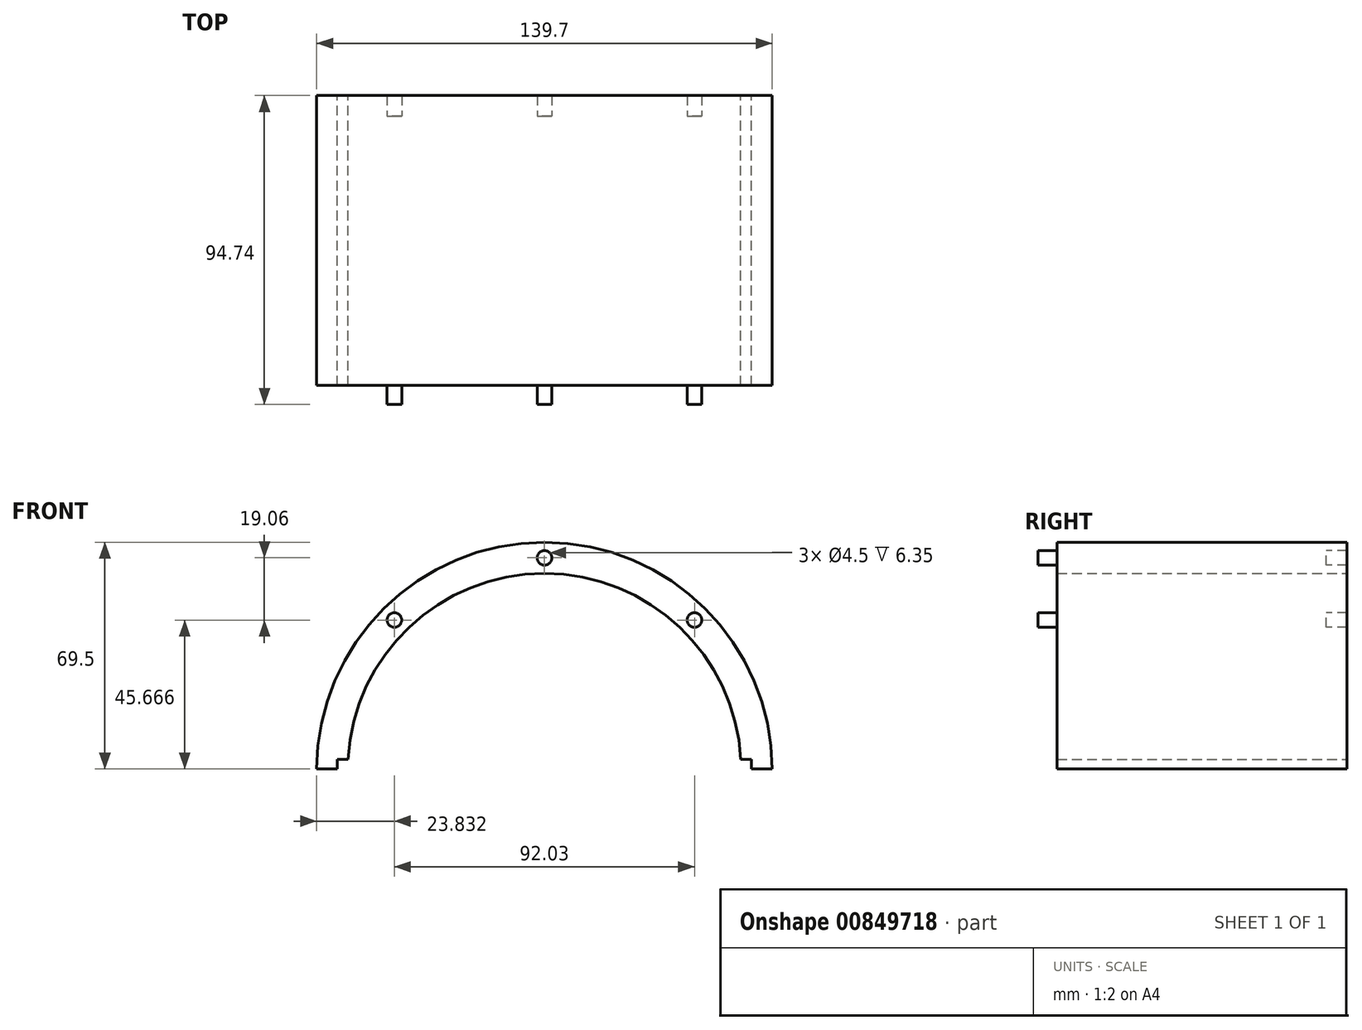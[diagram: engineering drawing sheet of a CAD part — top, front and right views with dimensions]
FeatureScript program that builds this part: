
annotation { "Feature Type Name" : "Feature", "Feature Type Description" : "" }
export const myFeature = defineFeature(function(context is Context, id is Id, definition is map)
    precondition{}
    {
        {
            var Q0;
            Q0=qCreatedBy(makeId("Front.planeOp"),FACE);
            var sketch = newSketch(context, id + "F0", { "sketchPlane" : qUnion([Q0])});
            skArc(sketch, "E0", {"start": v(33.34, 8.81) * mm, "mid": v(-36.51, 78.31) * mm, "end": v(-106.36, 8.81) * mm});
            skArc(sketch, "E1", {"start": v(23.72, 11.78) * mm, "mid": v(-36.51, 68.79) * mm, "end": v(-96.75, 11.78) * mm});
            skLineSegment(sketch, "E2.trimOffspring", {"start": v(26.98, 8.81) * mm, "end": v(33.34, 8.81) * mm});
            skLineSegment(sketch, "E3.left", {"start": v(-100, 11.78) * mm, "end": v(-100, 8.81) * mm});
            skLineSegment(sketch, "E4", {"start": v(-100, 11.78) * mm, "end": v(-96.75, 11.78) * mm});
            skLineSegment(sketch, "E5.right", {"start": v(26.98, 8.81) * mm, "end": v(26.98, 11.78) * mm});
            skLineSegment(sketch, "E6", {"start": v(-106.36, 8.81) * mm, "end": v(-100, 8.81) * mm});
            skPoint(sketch, "E7.orphan", {"position": v(27.73, 11.78) * mm});
            skLineSegment(sketch, "E8", {"start": v(26.98, 11.78) * mm, "end": v(23.72, 11.78) * mm});
            skLineSegment(sketch, "E9", {"start": v(26.98, 11.78) * mm, "end": v(33.26, 11.78) * mm});
            skLineSegment(sketch, "E10", {"start": v(-100, 11.78) * mm, "end": v(-106.28, 11.78) * mm});
            skLineSegment(sketch, "E11", {"start": v(26.98, 8.81) * mm, "end": v(-100, 8.81) * mm});
            skArc(sketch, "E12", {"start": v(30.16, 8.81) * mm, "mid": v(-36.51, 75.14) * mm, "end": v(-103.19, 8.81) * mm});
            skSolve(sketch);
        }
        {
            var Q0;
            Q0=makeQuery(id+"F0.imprint","IMPRINT",FACE,{"disambiguationData":[TD([[makeQuery(id+"F0.imprint","IMPRINT",EDGE,{"derivedFrom":sQuery(id+"F0.wireOp",EDGE,"E1")}),-1.0]])]});
            var Q1;
            Q1=makeQuery(id+"F0.imprint","IMPRINT",FACE,{"disambiguationData":[TD([[makeQuery(id+"F0.imprint","IMPRINT",EDGE,{"derivedFrom":sQuery(id+"F0.wireOp",EDGE,"E3.left")}),-1.0]])]});
            var Q2;
            {var subQ0=sQuery(id+"F0.wireOp",EDGE,"E2.trimOffspring");Q2=makeQuery(id+"F0.imprint","IMPRINT",FACE,{"disambiguationData":[TD([[makeQuery(id+"F0.imprint","IMPRINT",EDGE,{"derivedFrom":subQ0}),1.0]])]});}
            var Q3;
            {var subQ0=sQuery(id+"F0.wireOp",EDGE,"E9");var subQ1=sQuery(id+"F0.wireOp",EDGE,"E0");var subQ2=makeQuery(id+"F0.imprint","INTERSECT",VERTEX,{"derivedFrom":[subQ1,subQ0]});Q3=makeQuery(id+"F0.imprint","IMPRINT",FACE,{"disambiguationData":[TD([[makeQuery(id+"F0.imprint","IMPRINT",EDGE,{"disambiguationData":[TD([[subQ2,-1.0]])],"derivedFrom":subQ1}),1.0]])]});}
            var Q4;
            {var subQ0=sQuery(id+"F0.wireOp",EDGE,"E6");var subQ1=sQuery(id+"F0.wireOp",EDGE,"E0");var subQ2=makeQuery(id+"F0.imprint","INTERSECT",VERTEX,{"derivedFrom":[subQ1,subQ0]});Q4=makeQuery(id+"F0.imprint","IMPRINT",FACE,{"disambiguationData":[TD([[makeQuery(id+"F0.imprint","IMPRINT",EDGE,{"disambiguationData":[TD([[subQ2,1.0]])],"derivedFrom":subQ1}),1.0]])]});}
            extrude(context, id + "F1", {"entities" : qUnion([Q0, Q1, Q2, Q3, Q4]), "depth" : 88.9 * mm, "offsetDistance" : 25.4 * mm});
        }
        {
            var Q0;
            Q0=makeQuery(id+"F1.opExtrude","CAP_FACE",FACE,{"disambiguationData":[OSD([sQuery(id+"F0.wireOp",EDGE,"E0"),sQuery(id+"F0.wireOp",EDGE,"E1"),sQuery(id+"F0.wireOp",EDGE,"E2.trimOffspring"),sQuery(id+"F0.wireOp",EDGE,"E3.left"),sQuery(id+"F0.wireOp",EDGE,"E4"),sQuery(id+"F0.wireOp",EDGE,"E5.right"),sQuery(id+"F0.wireOp",EDGE,"E6"),sQuery(id+"F0.wireOp",EDGE,"E8")])],"isStart":false});
            var sketch = newSketch(context, id + "F2", { "sketchPlane" : qUnion([Q0])});
            skCircle(sketch, "E13", {"center": v(-82.53, 54.48) * mm, "radius": 2.25 * mm});
            skCircle(sketch, "E14", {"center": v(-36.51, 73.54) * mm, "radius": 2.25 * mm});
            skCircle(sketch, "E15", {"center": v(9.5, 54.48) * mm, "radius": 2.25 * mm});
            skSolve(sketch);
        }
        {
            var Q0;
            Q0=makeQuery(id+"F2.imprint","IMPRINT",FACE,{"disambiguationData":[TD([[makeQuery(id+"F2.imprint","IMPRINT",EDGE,{"derivedFrom":sQuery(id+"F2.wireOp",EDGE,"E14")}),1.0]])]});
            var Q1;
            Q1=makeQuery(id+"F2.imprint","IMPRINT",FACE,{"disambiguationData":[TD([[makeQuery(id+"F2.imprint","IMPRINT",EDGE,{"derivedFrom":sQuery(id+"F2.wireOp",EDGE,"E15")}),1.0]])]});
            var Q2;
            Q2=makeQuery(id+"F2.imprint","IMPRINT",FACE,{"disambiguationData":[TD([[makeQuery(id+"F2.imprint","IMPRINT",EDGE,{"derivedFrom":sQuery(id+"F2.wireOp",EDGE,"E13")}),1.0]])]});
            extrude(context, id + "F3", {"entities" : qUnion([Q0, Q1, Q2]), "operationType" : NewBodyOperationType.ADD, "depth" : 5.84 * mm, "offsetDistance" : 25.4 * mm});
        }
        {
            var Q0;
            Q0 = qSketchRegion(id + "F2", true);
            extrude(context, id + "F4", {"entities" : qUnion([Q0]), "operationType" : NewBodyOperationType.REMOVE, "oppositeDirection" : true, "depth" : 88.9 * mm, "offsetDistance" : 25.4 * mm, "hasSecondDirection" : true, "secondDirectionOppositeDirection" : true, "secondDirectionDepth" : 82.55 * mm});
        }
    });
